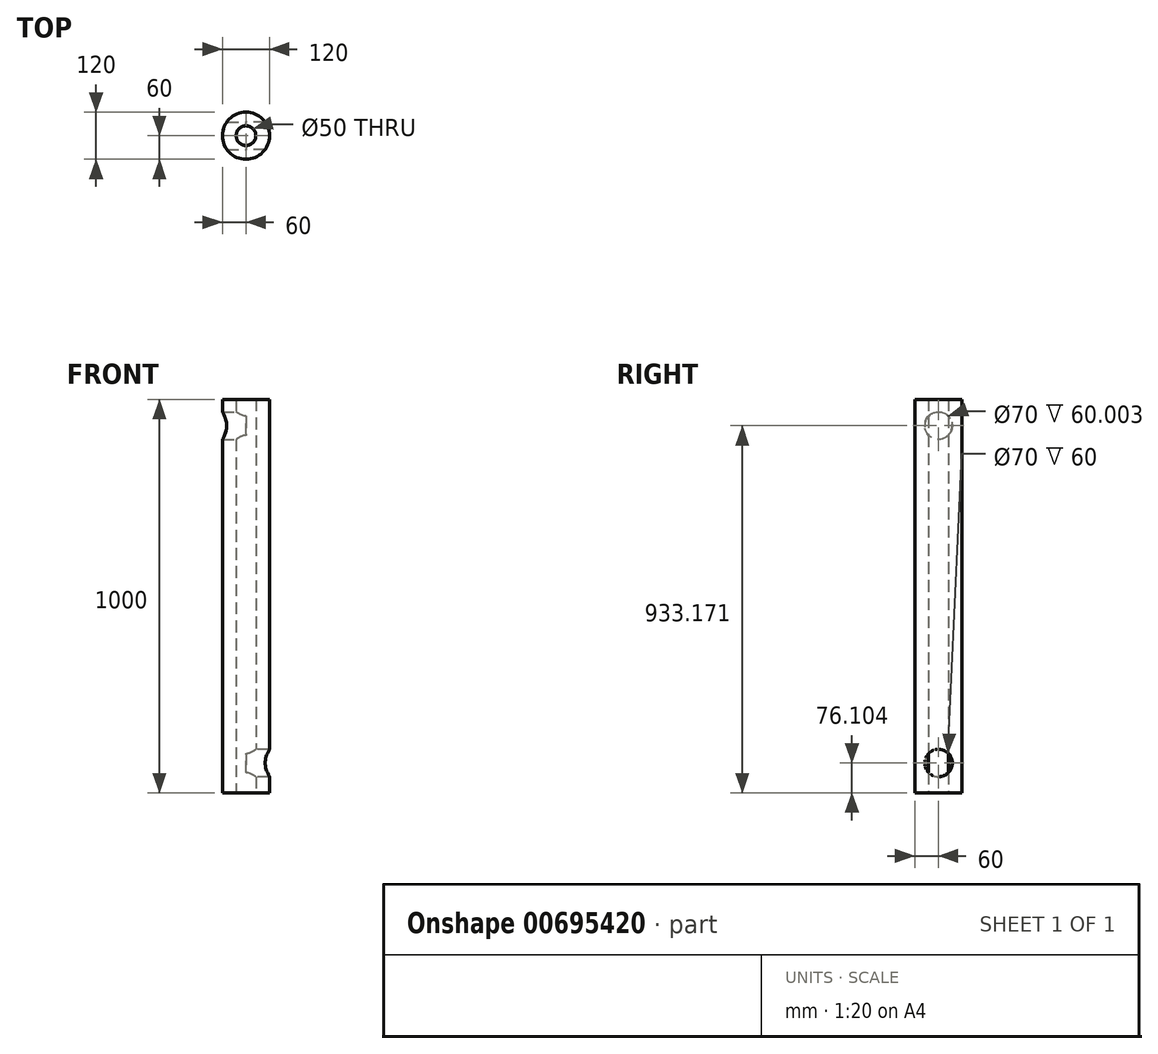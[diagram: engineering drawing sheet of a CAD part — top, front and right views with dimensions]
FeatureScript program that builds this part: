
annotation { "Feature Type Name" : "Feature", "Feature Type Description" : "" }
export const myFeature = defineFeature(function(context is Context, id is Id, definition is map)
    precondition{}
    {
        {
            var Q0;
            Q0=qCreatedBy(makeId("Top.planeOp"),FACE);
            var sketch = newSketch(context, id + "F0", { "sketchPlane" : qUnion([Q0])});
            skCircle(sketch, "E0", {"center": v(0, 0) * mm, "radius": 60 * mm});
            skCircle(sketch, "E1", {"center": v(0, 0) * mm, "radius": 25 * mm});
            skSolve(sketch);
        }
        {
            var Q0;
            Q0=makeQuery(id+"F0.imprint","IMPRINT",FACE,{"disambiguationData":[TD([[makeQuery(id+"F0.imprint","IMPRINT",EDGE,{"derivedFrom":sQuery(id+"F0.wireOp",EDGE,"E0")}),1.0]])]});
            extrude(context, id + "F1", {"entities" : qUnion([Q0]), "endBound" : BoundingType.SYMMETRIC, "depth" : 1000 * mm, "offsetDistance" : 25 * mm});
        }
        {
            var Q0;
            Q0=qCreatedBy(makeId("Right.planeOp"),FACE);
            var sketch = newSketch(context, id + "F2", { "sketchPlane" : qUnion([Q0])});
            skCircle(sketch, "E2", {"center": v(0, 433.17) * mm, "radius": 35 * mm});
            skPoint(sketch, "E3.center.orphan", {"position": v(0, -431.49) * mm});
            skSolve(sketch);
        }
        {
            var Q0;
            Q0=sQuery(id+"F2.wireOp",VERTEX,"E2.center");
            var Q1;
            Q1=makeQuery(id+"F1.opExtrude","SWEPT_BODY",BODY,{"disambiguationData":[OSD([sQuery(id+"F0.wireOp",EDGE,"E0"),sQuery(id+"F0.wireOp",EDGE,"E1")])]});
            hole(context, id + "F3", {"style" : HoleStyle.SIMPLE, "endStyle" : HoleEndStyle.THROUGH, "holeDiameter" : 70 * mm, "majorDiameter" : 5 * mm, "isTappedThrough" : true, "tappedDepth" : 12 * mm, "tapClearance" : 3, "locations" : qUnion([Q0]), "scope" : qUnion([Q1])});
        }
        {
            var Q0;
            Q0=qCreatedBy(makeId("Right.planeOp"),FACE);
            var sketch = newSketch(context, id + "F4", { "sketchPlane" : qUnion([Q0])});
            skCircle(sketch, "E4", {"center": v(0, -423.9) * mm, "radius": 34.77 * mm});
            skSolve(sketch);
        }
        {
            var Q0;
            Q0=sQuery(id+"F4.wireOp",VERTEX,"E4.center");
            var Q1;
            Q1=makeQuery(id+"F1.opExtrude","SWEPT_BODY",BODY,{"disambiguationData":[OSD([sQuery(id+"F0.wireOp",EDGE,"E0"),sQuery(id+"F0.wireOp",EDGE,"E1")])]});
            hole(context, id + "F5", {"style" : HoleStyle.SIMPLE, "endStyle" : HoleEndStyle.THROUGH, "oppositeDirection" : true, "holeDiameter" : 70 * mm, "majorDiameter" : 5 * mm, "isTappedThrough" : true, "tappedDepth" : 12 * mm, "tapClearance" : 3, "locations" : qUnion([Q0]), "scope" : qUnion([Q1])});
        }
    });
